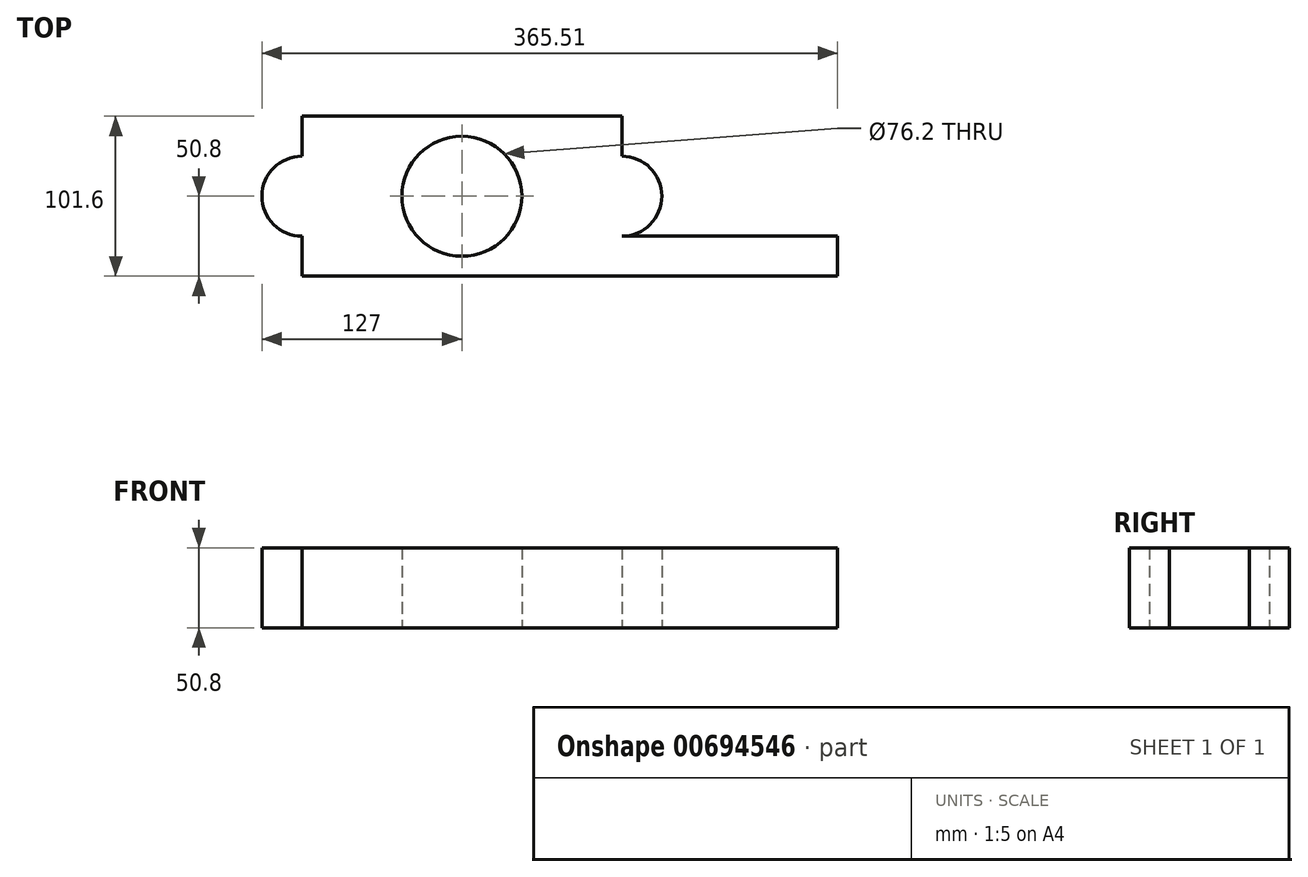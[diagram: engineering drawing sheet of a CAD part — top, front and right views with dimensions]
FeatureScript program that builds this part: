
annotation { "Feature Type Name" : "Feature", "Feature Type Description" : "" }
export const myFeature = defineFeature(function(context is Context, id is Id, definition is map)
    precondition{}
    {
        {
            var Q0;
            Q0=qCreatedBy(makeId("Top.planeOp"),FACE);
            var sketch = newSketch(context, id + "F0", { "sketchPlane" : qUnion([Q0])});
            skLineSegment(sketch, "E0.bottom", {"start": v(-101.6, 50.8) * mm, "end": v(101.6, 50.8) * mm});
            skLineSegment(sketch, "E0.top", {"start": v(-101.6, -50.8) * mm, "end": v(101.6, -50.8) * mm});
            skLineSegment(sketch, "E0.left", {"start": v(-101.6, 50.8) * mm, "end": v(-101.6, 25.4) * mm});
            skLineSegment(sketch, "E0.right", {"start": v(101.6, 50.8) * mm, "end": v(101.6, 25.4) * mm});
            skCircle(sketch, "E1", {"center": v(0, 0) * mm, "radius": 38.1 * mm});
            skArc(sketch, "E2", {"start": v(-101.6, 25.4) * mm, "mid": v(-127, 0) * mm, "end": v(-101.6, -25.4) * mm});
            skArc(sketch, "E3", {"start": v(101.6, -25.4) * mm, "mid": v(127, 0) * mm, "end": v(101.6, 25.4) * mm});
            skLineSegment(sketch, "E4.trimOffspring", {"start": v(101.6, -25.4) * mm, "end": v(101.6, -50.8) * mm});
            skLineSegment(sketch, "E5.trimOffspring", {"start": v(-101.6, -25.4) * mm, "end": v(-101.6, -50.8) * mm});
            skSolve(sketch);
        }
        {
            var Q0;
            Q0=makeQuery(id+"F0.imprint","IMPRINT",FACE,{"disambiguationData":[TD([[makeQuery(id+"F0.imprint","IMPRINT",EDGE,{"derivedFrom":sQuery(id+"F0.wireOp",EDGE,"E0.bottom")}),-1.0]])]});
            extrude(context, id + "F1", {"entities" : qUnion([Q0]), "depth" : 50.8 * mm, "offsetDistance" : 25.4 * mm});
        }
        {
            var Q0;
            Q0=makeQuery(id+"F1.opExtrude","SWEPT_FACE",FACE,{"disambiguationData":[OSD([sQuery(id+"F0.wireOp",EDGE,"E4.trimOffspring")])]});
            extrude(context, id + "F2", {"entities" : qUnion([Q0]), "operationType" : NewBodyOperationType.ADD, "depth" : 136.9 * mm, "offsetDistance" : 25.4 * mm});
        }
    });
